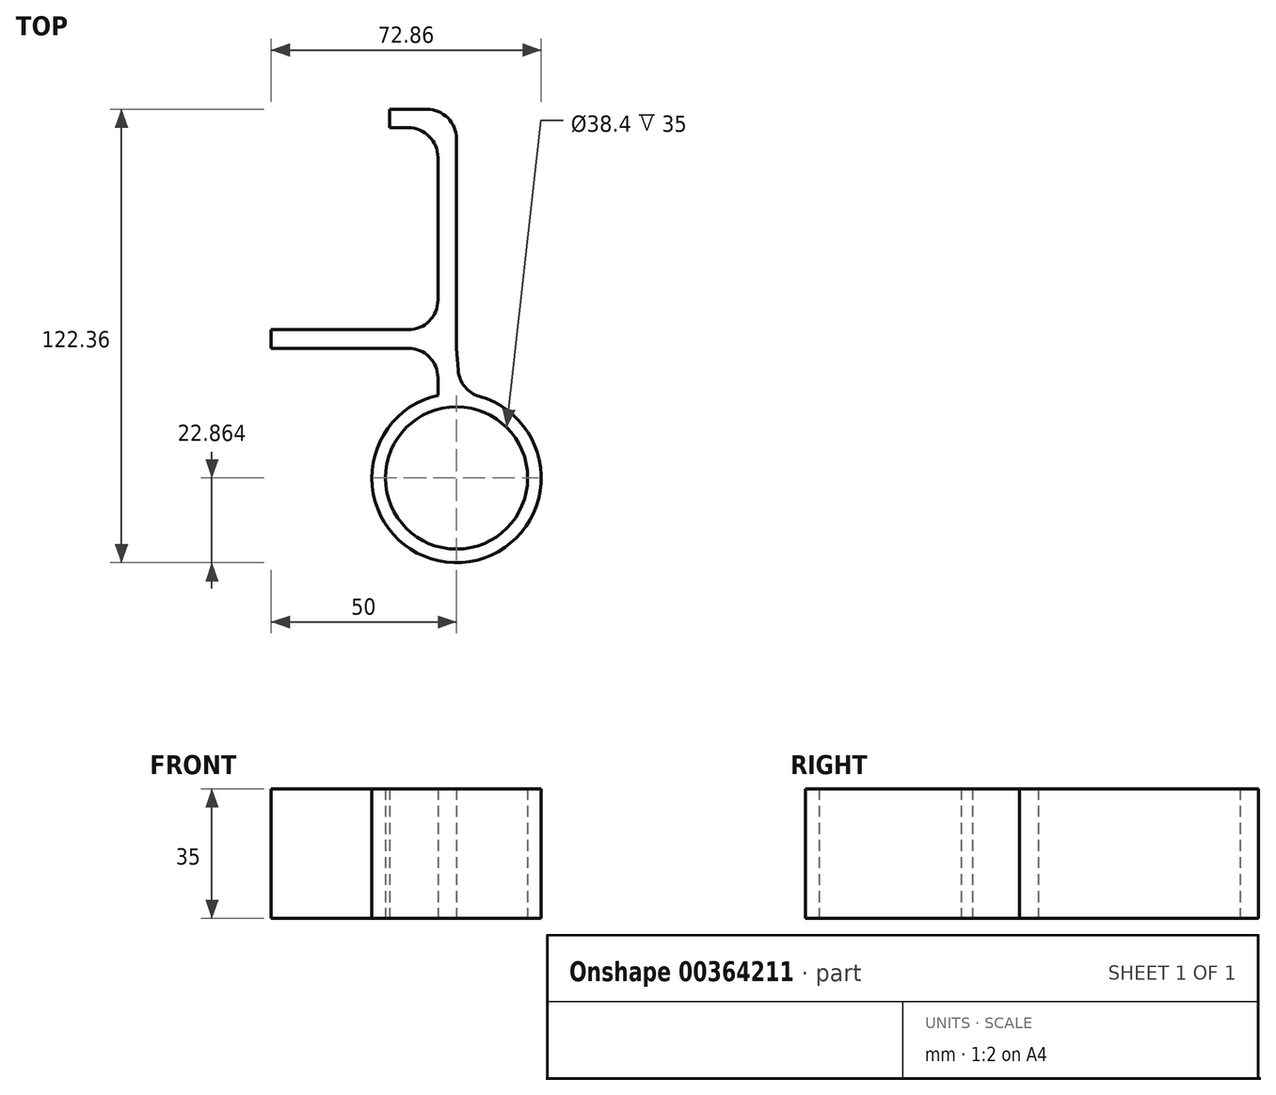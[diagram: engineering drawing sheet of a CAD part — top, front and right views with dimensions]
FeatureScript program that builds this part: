
annotation { "Feature Type Name" : "Feature", "Feature Type Description" : "" }
export const myFeature = defineFeature(function(context is Context, id is Id, definition is map)
    precondition{}
    {
        {
            var Q0;
            Q0=qCreatedBy(makeId("Top.planeOp"),FACE);
            var sketch = newSketch(context, id + "F0", { "sketchPlane" : qUnion([Q0])});
            skLineSegment(sketch, "E0.bottom", {"start": v(-45, -7.87) * mm, "end": v(0, -7.87) * mm});
            skLineSegment(sketch, "E0.top", {"start": v(-45, -2.87) * mm, "end": v(-8, -2.87) * mm});
            skLineSegment(sketch, "E0.left", {"start": v(-45, -7.87) * mm, "end": v(-45, -2.87) * mm});
            skLineSegment(sketch, "E0.right", {"start": v(0, 5.13) * mm, "end": v(0, 43.63) * mm});
            skLineSegment(sketch, "E1.top", {"start": v(-8, -7.87) * mm, "end": v(-45, -7.87) * mm});
            skLineSegment(sketch, "E1.left", {"start": v(5, 48.63) * mm, "end": v(5, -7.87) * mm});
            skLineSegment(sketch, "E1.right", {"start": v(-45, -2.87) * mm, "end": v(-45, -7.87) * mm});
            skArc(sketch, "E2", {"start": v(0, -20.56) * mm, "mid": v(4.36, -65.72) * mm, "end": v(11.25, -20.88) * mm});
            skLineSegment(sketch, "E3", {"start": v(0, -15.87) * mm, "end": v(0, -20.56) * mm});
            skLineSegment(sketch, "E4", {"start": v(5.46, -13.8) * mm, "end": v(5, -7.87) * mm});
            skCircle(sketch, "E5", {"center": v(5, -42.87) * mm, "radius": 19.2 * mm});
            skPoint(sketch, "E6.visualSharp", {"position": v(0, -2.87) * mm});
            skArc(sketch, "E6.filletArc", {"start": v(-8, -2.87) * mm, "mid": v(-2.34, -0.52) * mm, "end": v(0, 5.13) * mm});
            skPoint(sketch, "E7.newPointA", {"position": v(5, -7.87) * mm});
            skArc(sketch, "E7.filletArc", {"start": v(0, -15.87) * mm, "mid": v(-2.34, -10.2) * mm, "end": v(-8, -7.87) * mm});
            skPoint(sketch, "E8.visualSharp", {"position": v(5.93, -20.03) * mm});
            skArc(sketch, "E8.filletArc", {"start": v(5.46, -13.8) * mm, "mid": v(7.24, -18.24) * mm, "end": v(11.25, -20.88) * mm});
            skLineSegment(sketch, "E9", {"start": v(-8, 51.63) * mm, "end": v(-13, 51.63) * mm});
            skLineSegment(sketch, "E10", {"start": v(-13, 51.63) * mm, "end": v(-13, 56.63) * mm});
            skLineSegment(sketch, "E11", {"start": v(-13, 56.63) * mm, "end": v(-3, 56.63) * mm});
            skPoint(sketch, "E12.visualSharp", {"position": v(0, 51.63) * mm});
            skArc(sketch, "E12.filletArc", {"start": v(0, 43.63) * mm, "mid": v(-2.34, 49.3) * mm, "end": v(-8, 51.63) * mm});
            skPoint(sketch, "E13.newPointB", {"position": v(5, 46.13) * mm});
            skArc(sketch, "E13.filletArc", {"start": v(5, 48.63) * mm, "mid": v(2.66, 54.3) * mm, "end": v(-3, 56.63) * mm});
            skSolve(sketch);
        }
        {
            var Q0;
            Q0 = qSketchRegion(id + "F0", true);
            extrude(context, id + "F1", {"entities" : qUnion([Q0]), "depth" : 35 * mm});
        }
    });
